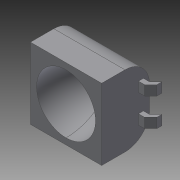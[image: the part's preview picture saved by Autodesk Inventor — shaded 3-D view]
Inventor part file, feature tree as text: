
AUTODESK INVENTOR PART (.ipt)
format: ipt  version: 2014 SP2 (Build 180246200, 246)  size: 211,456 bytes
history: native  units: mm
features: sketch x4, extrude x3, mirror x2, other x1, revolve x1, fillet x1, projected_geometry x1
ambient origin geometry x8: Origin, YZ Plane, XZ Plane, XY Plane, X Axis, Y Axis, Z Axis, Center Point
bodies: Solid1 (feature_tree)
feature tree (13):
  extrude  "Extrusion1"  Depth=58.0mm
  other  "Work Axis1"
  revolve  "Revolution1"  [1 undecoded]
  extrude  "Extrusion2"  TaperAngle=90.0deg  [1 undecoded]
  extrude  "Extrusion3"  Depth=4.0mm
  mirror  "Mirror1"
  mirror  "Mirror2"
  fillet  "Fillet1"  Radius=15.0mm
  sketch  "Sketch1"  dims[d0=58.0mm d1=58.0mm]
  sketch  "Sketch2"  dims[d2=39.0mm d3=0.0mm d5=33.0mm]
  sketch  "Sketch3"  dims[d6=24.0mm d7=90.0deg]
  sketch  "Sketch6"  dims[d8=8.0mm d9=4.0mm d10=15.0mm d11=5.0mm d12=0.0mm d14=5.0mm d18=45.0deg d19=4.0mm d20=0.0mm d21=0.0mm d22=20.0mm]
  projected_geometry  "Projected Loop3"
note: 2 required parameter values undecoded (feature->parameter linkage not recoverable at this tier; creation-order binding heuristic only, values carry confidence <= 0.55)